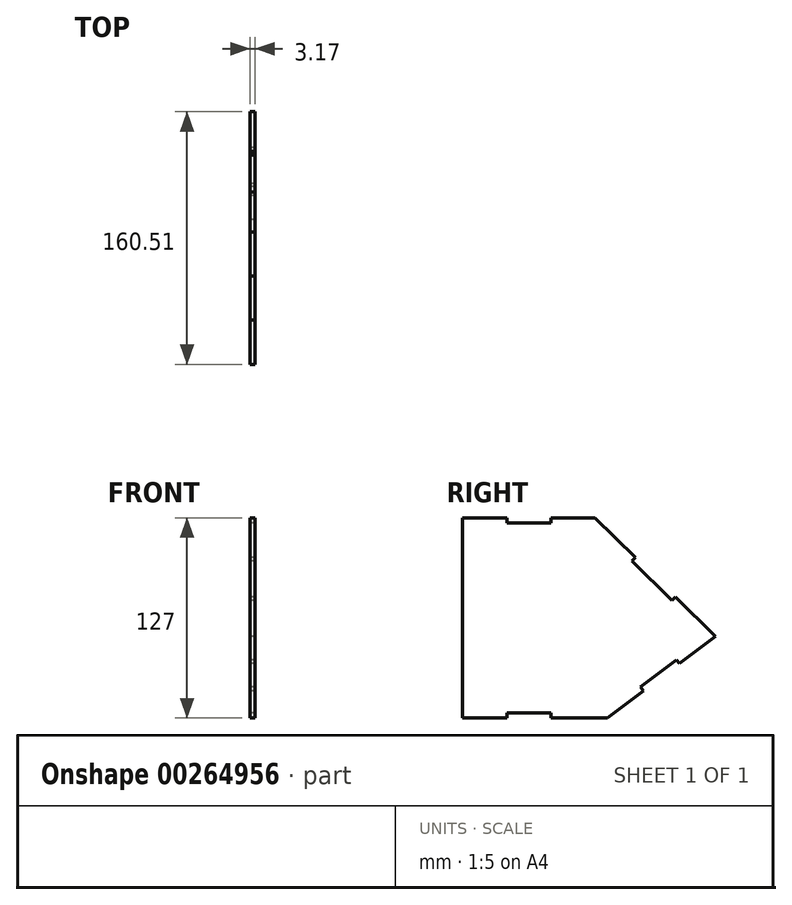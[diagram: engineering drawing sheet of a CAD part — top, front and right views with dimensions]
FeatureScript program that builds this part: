
annotation { "Feature Type Name" : "Feature", "Feature Type Description" : "" }
export const myFeature = defineFeature(function(context is Context, id is Id, definition is map)
    precondition{}
    {
        {
            var Q0;
            Q0=qCreatedBy(makeId("Right.planeOp"),FACE);
            var sketch = newSketch(context, id + "F0", { "sketchPlane" : qUnion([Q0])});
            skLineSegment(sketch, "E0", {"start": v(-48.2, 0) * mm, "end": v(-48.2, 63.5) * mm});
            skLineSegment(sketch, "E1", {"start": v(-48.2, 63.5) * mm, "end": v(-20.15, 63.5) * mm});
            skLineSegment(sketch, "E2.MirrorCS", {"start": v(-48.2, 0) * mm, "end": v(-48.2, -63.5) * mm});
            skLineSegment(sketch, "E3.MirrorCS", {"start": v(-48.2, -63.5) * mm, "end": v(-20.15, -63.5) * mm});
            skLineSegment(sketch, "E4", {"start": v(43.88, -63.5) * mm, "end": v(66.69, -46.29) * mm});
            skLineSegment(sketch, "E5", {"start": v(35.94, 63.5) * mm, "end": v(61.4, 38.38) * mm});
            skLineSegment(sketch, "E6", {"start": v(-48.2, 63.5) * mm, "end": v(-48.2, 60.33) * mm});
            skLineSegment(sketch, "E7", {"start": v(-20.15, 60.33) * mm, "end": v(7.9, 60.33) * mm});
            skLineSegment(sketch, "E8", {"start": v(-20.15, 63.5) * mm, "end": v(-20.15, 60.33) * mm});
            skLineSegment(sketch, "E9", {"start": v(7.9, 63.5) * mm, "end": v(7.9, 60.33) * mm});
            skLineSegment(sketch, "E10.trimOffspring", {"start": v(7.9, 63.5) * mm, "end": v(35.94, 63.5) * mm});
            skPoint(sketch, "E11.orphan", {"position": v(35.94, 60.33) * mm});
            skLineSegment(sketch, "E12", {"start": v(-20.15, -60.32) * mm, "end": v(-20.15, -63.5) * mm});
            skLineSegment(sketch, "E13", {"start": v(-20.15, -63.5) * mm, "end": v(-20.15, -60.32) * mm});
            skLineSegment(sketch, "E14", {"start": v(7.9, -60.32) * mm, "end": v(7.9, -63.5) * mm});
            skLineSegment(sketch, "E15", {"start": v(-20.15, -60.32) * mm, "end": v(7.9, -60.32) * mm});
            skLineSegment(sketch, "E16.trimOffspring", {"start": v(7.9, -63.5) * mm, "end": v(43.88, -63.5) * mm});
            skPoint(sketch, "E17.end.orphan", {"position": v(35.94, -60.32) * mm});
            skLineSegment(sketch, "E18", {"start": v(61.4, 38.38) * mm, "end": v(59.17, 36.12) * mm});
            skLineSegment(sketch, "E19", {"start": v(59.17, 36.12) * mm, "end": v(84.62, 11) * mm});
            skLineSegment(sketch, "E20", {"start": v(86.85, 13.26) * mm, "end": v(84.62, 11) * mm});
            skLineSegment(sketch, "E21.trimOffspring", {"start": v(86.85, 13.26) * mm, "end": v(112.3, -11.86) * mm});
            skLineSegment(sketch, "E22", {"start": v(112.3, -11.86) * mm, "end": v(89.5, -29.07) * mm});
            skLineSegment(sketch, "E23", {"start": v(89.5, -29.07) * mm, "end": v(87.58, -26.54) * mm});
            skLineSegment(sketch, "E24", {"start": v(87.58, -26.54) * mm, "end": v(64.78, -43.75) * mm});
            skLineSegment(sketch, "E25", {"start": v(66.69, -46.29) * mm, "end": v(64.78, -43.75) * mm});
            skLineSegment(sketch, "E26.trimOffspring", {"start": v(89.5, -29.07) * mm, "end": v(112.3, -11.86) * mm});
            skSolve(sketch);
        }
        {
            var Q0;
            Q0=makeQuery(id+"F0.imprint","IMPRINT",FACE,{"disambiguationData":[TD([[makeQuery(id+"F0.imprint","IMPRINT",EDGE,{"derivedFrom":sQuery(id+"F0.wireOp",EDGE,"E0")}),-1.0]])]});
            extrude(context, id + "F1", {"entities" : qUnion([Q0]), "depth" : 3.17 * mm});
        }
    });
